# Revit family: ARGOWALL-DD-LP-HVG_UKS02820210001
name_source: partatom
category: Lighting Fixtures
units: mm (PartAtom-declared; Revit-internal decimal feet)

## family parameters
Cut with Voids When Loaded = No
Host = Face
Light Source = Yes
Part Type = Normal
Room Calculation Point = No
Round Connector Dimension = Use Diameter
Shared = No

## types (1)
- ARGOWALL-DD-LP-HVG-UKS02820210001
    Apparent Load = 21 VA
    Clevertronics_Annotation Size = 0 mm  [stored 0 ft]
    Clevertronics_Battery Type = Lithium Nanophosphate (LiFePO4), Clevertronics
    Clevertronics_Charger Method = Intelligent Current Limited Constant Voltage
    Clevertronics_Conformity = BS EN 60598.2.22, BS 5266
    Clevertronics_Construction = Die Cast Aluminium Body with Polycarbonate LED Cover
    Clevertronics_Diffuser = Polycarbonate with asymmetric lenses over the LEDs to suit wall mounted,
walkway, applications (LED cover fitted with 4 security torx head screws)
    Clevertronics_Dimensions Main Enclosure = 305mm (W) x 310mm (H) x 155mm (D)
    Clevertronics_Earth Leakage = 0.224mA
    Clevertronics_Emergency Driver = UKM02870330001
    Clevertronics_HIVE Node = 8003645
    Clevertronics_Height = 310 mm  [stored 1.01706 ft]
    Clevertronics_IK Rating = IK10
    Clevertronics_IP Rating = IP65
    Clevertronics_Inrush Current = 6.24A / 172 μs
    Clevertronics_LED Assembly = 8050219
    Clevertronics_LED Driver = 1330045
    Clevertronics_Length = 155 mm  [stored 0.50853 ft]
    Clevertronics_Luminaire Classification = X | 0 | ADF | 180
    Clevertronics_MIC Number = UKS02820210001
    Clevertronics_Material = Clevertronics_Plycarbonate Base
    Clevertronics_Mounting = Surface Mount (Wall, with LED light source facing downwards)
    Clevertronics_Operating Mode = Maintained (with integrated photocell for automatic on/off operation depending on
ambient light levels)
    Clevertronics_Operating Temperature = 0˚C to 40˚C
    Clevertronics_Operating Voltage = 220-240V AC; 50Hz
    Clevertronics_Power Consumption = 19.9W (Lamps ON Max Charge), 15.8W (Lamps ON Standby), 1.4W (Lamps OFF Standby)
1.7W (Lamps OFF Standby)
    Clevertronics_Power factor = 0.9
    Clevertronics_Product Description = Argonaut Wall Light IP65 Weatherproof Emergency, Surface Mount, L10 Nanophosphate, Maintained, Zoneworks XT Hive, Anthracite Grey (RAL7016)
    Clevertronics_Rated Emergency Duration = 180 minutes
    Clevertronics_Replacement Battery = 1553290
    Clevertronics_Supply Current = 111mA (Lamps ON Max Charge), 89mA (Lamps ON Standby)
    Clevertronics_Testing System = Zoneworks XT HIVE (RF) 2.4GHz
    Clevertronics_Total Lumen Output = 1646
    Clevertronics_Weight = 4.6Kg
    Clevertronics_Width = 305 mm  [stored 1.00066 ft]
    Color Filter = 16777215
    Default Elevation = 0 mm  [stored 0 ft]
    Description = Argonaut Wall Light IP65 Weatherproof Emergency, Surface Mount, L10 Nanophosphate, Maintained, Zoneworks XT Hive, Anthracite Grey (RAL7016)
    Dimming Lamp Color Temperature Shift = <None>
    Lamp = LED module, 4000K, 100,000h [L70/ B50, Ta 40°C], Ra>80
    Manufacturer = Clevertronics
    Model = ARGOWALL-DD-LP-HVG
    Photometric Web File = OEM_CLEVERWALL_1_IESD_E_202211211213.IES
    Tilt Angle = 180.00°

note: [stored X ft] marks values corroborated as IEEE doubles in the binary element streams (Revit-internal decimal feet)

## geometry (parser evidence)
native form markers: Blend x2, Sweep x1
no freeform markers — native parametric forms only
